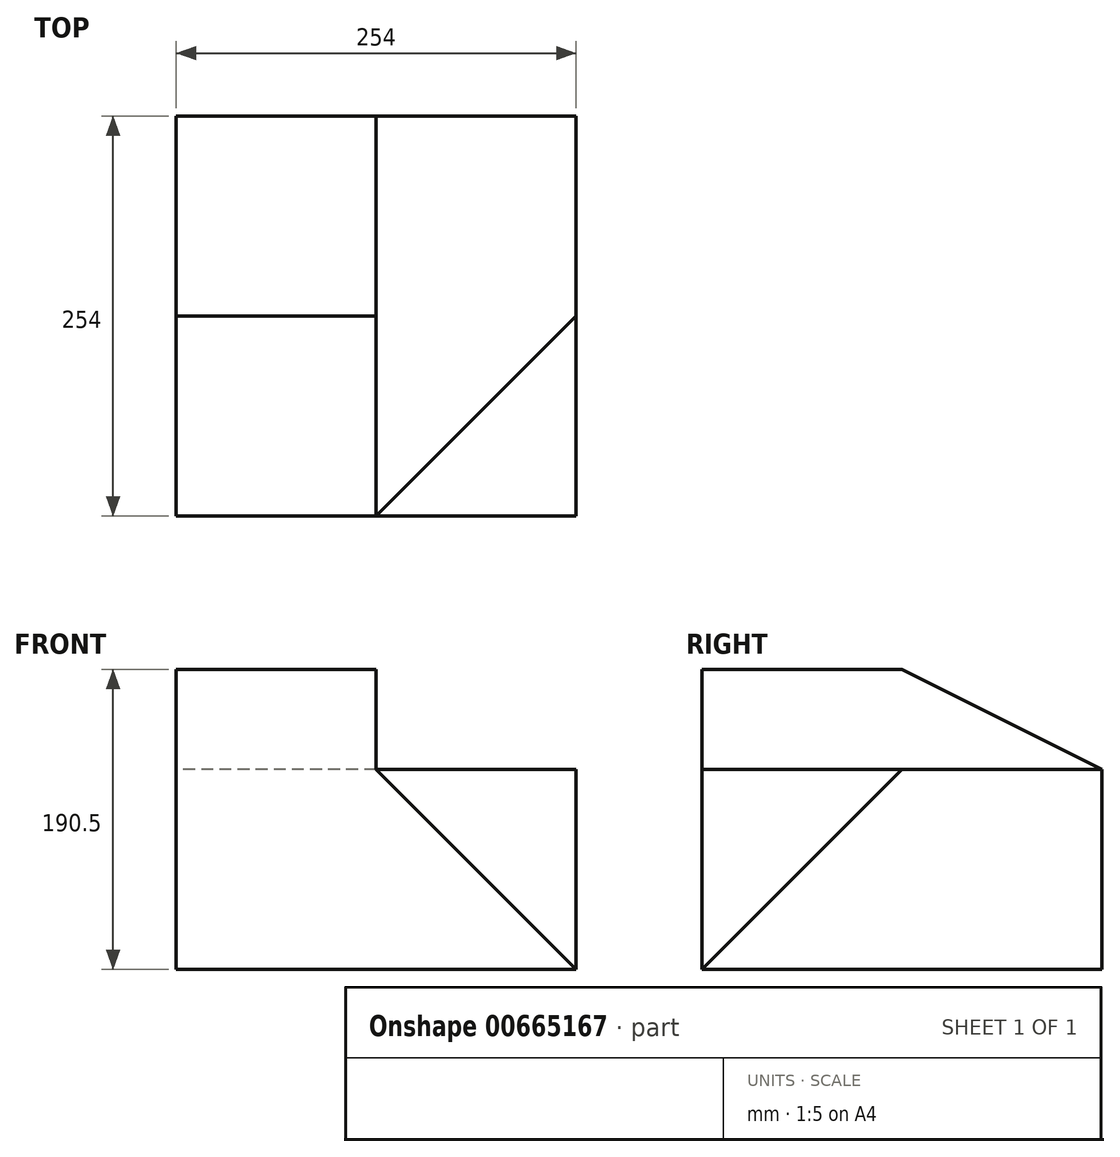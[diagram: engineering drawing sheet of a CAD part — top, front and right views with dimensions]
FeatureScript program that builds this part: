
annotation { "Feature Type Name" : "Feature", "Feature Type Description" : "" }
export const myFeature = defineFeature(function(context is Context, id is Id, definition is map)
    precondition{}
    {
        {
            var Q0;
            Q0=qCreatedBy(makeId("Front.planeOp"),FACE);
            var sketch = newSketch(context, id + "F0", { "sketchPlane" : qUnion([Q0])});
            skLineSegment(sketch, "E0", {"start": v(0, 0) * mm, "end": v(0, 190.5) * mm});
            skLineSegment(sketch, "E1", {"start": v(0, 190.5) * mm, "end": v(127, 190.5) * mm});
            skLineSegment(sketch, "E2", {"start": v(127, 190.5) * mm, "end": v(127, 127) * mm});
            skLineSegment(sketch, "E3", {"start": v(127, 127) * mm, "end": v(254, 127) * mm});
            skLineSegment(sketch, "E4", {"start": v(254, 127) * mm, "end": v(254, 0) * mm});
            skLineSegment(sketch, "E5", {"start": v(254, 0) * mm, "end": v(0, 0) * mm});
            skSolve(sketch);
        }
        {
            var Q0;
            Q0 = qSketchRegion(id + "F0", true);
            extrude(context, id + "F1", {"entities" : qUnion([Q0]), "endBound" : BoundingType.SYMMETRIC, "depth" : 254 * mm, "offsetDistance" : 25.4 * mm});
        }
        {
            var Q0;
            Q0=makeQuery(id+"F1.opExtrude","SWEPT_FACE",FACE,{"disambiguationData":[OSD([sQuery(id+"F0.wireOp",EDGE,"E0")])]});
            var sketch = newSketch(context, id + "F2", { "sketchPlane" : qUnion([Q0])});
            skLineSegment(sketch, "E6", {"start": v(0, 190.5) * mm, "end": v(-127, 127) * mm});
            skSolve(sketch);
        }
        {
            var Q0;
            {var subQ0=sQuery(id+"F2.wireOp",EDGE,"E6");Q0=makeQuery(id+"F2.imprint","IMPRINT",FACE,{"disambiguationData":[TD([[makeQuery(id+"F2.imprint","IMPRINT",EDGE,{"derivedFrom":subQ0}),-1.0]])]});}
            extrude(context, id + "F3", {"entities" : qUnion([Q0]), "operationType" : NewBodyOperationType.REMOVE, "oppositeDirection" : true, "depth" : 127 * mm, "offsetDistance" : 25.4 * mm});
        }
        {
            var Q0;
            Q0=makeQuery(id+"F1.opExtrude","SWEPT_EDGE",EDGE,{"disambiguationData":[OSD([sQuery(id+"F0.wireOp",EDGE,"E3"),sQuery(id+"F0.wireOp",EDGE,"E4")])]});
            cPoint(context, id + "F4", {"entities" : qUnion([Q0]), "parameter" : 0.5});
        }
        {
            var Q0;
            Q0=makeQuery(id+"F1.opExtrude","CAP_VERTEX",VERTEX,{"disambiguationData":[OSD([sQuery(id+"F0.wireOp",EDGE,"E2"),sQuery(id+"F0.wireOp",EDGE,"E3")])],"isStart":false});
            var Q1;
            Q1 = qCreatedBy(id + "F4" ,VERTEX);
            var Q2;
            Q2=makeQuery(id+"F1.opExtrude","CAP_VERTEX",VERTEX,{"disambiguationData":[OSD([sQuery(id+"F0.wireOp",EDGE,"E4"),sQuery(id+"F0.wireOp",EDGE,"E5")])],"isStart":false});
            cPlane(context, id + "F5", {"entities" : qUnion([Q0, Q1, Q2]), "cplaneType" : CPlaneType.THREE_POINT, "offset" : 25.4 * mm, "width" : 152.4 * mm, "height" : 152.4 * mm});
        }
        {
            var Q0;
            Q0=qCreatedBy(id+"F5.planeOp",FACE);
            var sketch = newSketch(context, id + "F6", { "sketchPlane" : qUnion([Q0])});
            skLineSegment(sketch, "E7", {"start": v(0, 0) * mm, "end": v(155.54, -89.8) * mm});
            skLineSegment(sketch, "E8", {"start": v(155.54, 89.8) * mm, "end": v(0, 0) * mm});
            skLineSegment(sketch, "E9", {"start": v(155.54, -89.8) * mm, "end": v(155.54, 89.8) * mm});
            skSolve(sketch);
        }
        {
            var Q0;
            Q0 = qSketchRegion(id + "F6", true);
            extrude(context, id + "F7", {"entities" : qUnion([Q0]), "operationType" : NewBodyOperationType.REMOVE, "depth" : 277.88 * mm, "offsetDistance" : 25.4 * mm});
        }
    });
